# Revit family: H1000-TR011
name_source: partatom
category: Aparatos sanitarios
units: mm (PartAtom-declared; Revit-internal decimal feet)

## family parameters
Compartido = No
Corte con vacíos al cargar = No
Cota de conector redondo = Diámetro de uso
Número OmniClass = 23.45.00.00
Punto de cálculo de habitación = No
Se basa en plano de trabajo = No
Siempre vertical = Sí
Tipo de pieza = Normal
Título OmniClass = Sanitary, Laundry, and Cleaning Equipment

## types (2) — shared parameters
Brass Chromed = Brass
Comentarios de tipo = Showerheads
Compliance = NOM-008-CONAGUA-1998
Descripción = Regadera de chorro regulable con palanca de 
control, brazo y chapetón.
Elevación por defecto = 75"
Fabricante = HELVEX
Inlet Threads = ½" - 14 NPT
Max. Working Pressure = 85.3 psi
Min. Working Pressure = 14.2 psi
Modelo = H1000-TR011
Total Length = 8"
Total Width = 2"

## type names (no varying parameters)
- AC50-TR011
- H1000-TR011

## geometry (parser evidence)
native form markers: Sweep x3
no freeform markers — native parametric forms only
